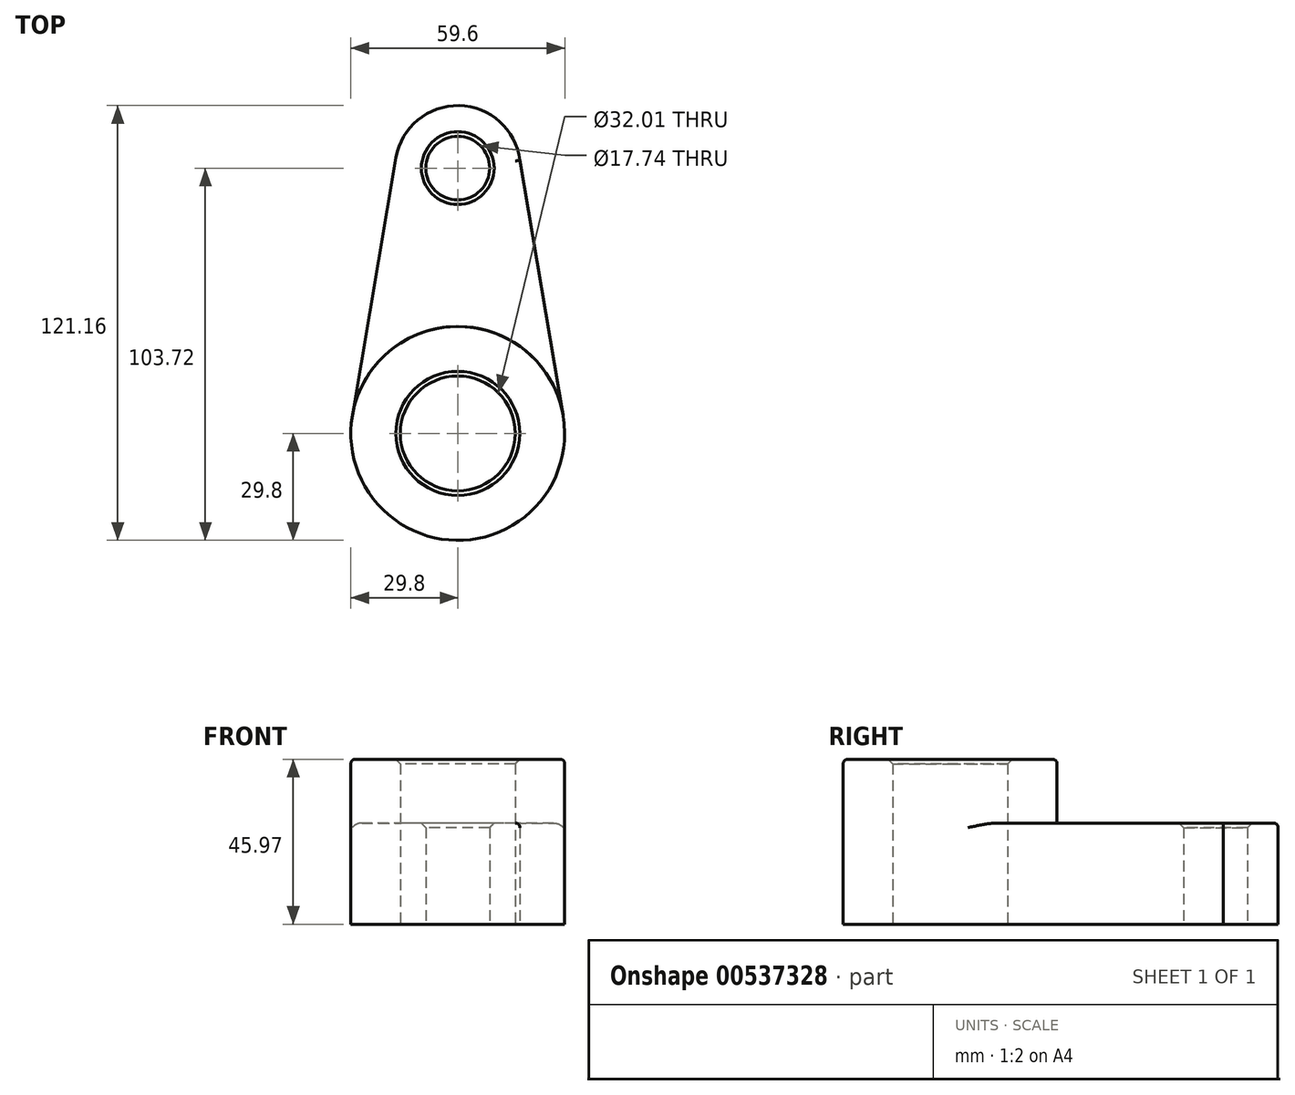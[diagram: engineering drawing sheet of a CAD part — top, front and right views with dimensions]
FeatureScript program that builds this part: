
annotation { "Feature Type Name" : "Feature", "Feature Type Description" : "" }
export const myFeature = defineFeature(function(context is Context, id is Id, definition is map)
    precondition{}
    {
        {
            var Q0;
            Q0=qCreatedBy(makeId("Top.planeOp"),FACE);
            var sketch = newSketch(context, id + "F0", { "sketchPlane" : qUnion([Q0])});
            skCircle(sketch, "E0", {"center": v(0, 0) * mm, "radius": 29.8 * mm});
            skCircle(sketch, "E1", {"center": v(0, 0) * mm, "radius": 16 * mm});
            skCircle(sketch, "E2", {"center": v(0, 73.92) * mm, "radius": 17.44 * mm});
            skCircle(sketch, "E3", {"center": v(0, 73.92) * mm, "radius": 8.87 * mm});
            skLineSegment(sketch, "E4", {"start": v(-29.38, 4.98) * mm, "end": v(-17.2, 76.84) * mm});
            skLineSegment(sketch, "E5", {"start": v(17.3, 76.1) * mm, "end": v(29.38, 4.99) * mm});
            skSolve(sketch);
        }
        {
            var Q0;
            Q0 = qSketchRegion(id + "F0", true);
            extrude(context, id + "F1", {"entities" : qUnion([Q0]), "depth" : 28.2 * mm, "offsetDistance" : 25.4 * mm});
        }
        {
            var Q0;
            Q0=makeQuery(id+"F0.imprint","IMPRINT",FACE,{"disambiguationData":[TD([[makeQuery(id+"F0.imprint","IMPRINT",EDGE,{"derivedFrom":sQuery(id+"F0.wireOp",EDGE,"E1")}),-1.0]])]});
            extrude(context, id + "F2", {"entities" : qUnion([Q0]), "operationType" : NewBodyOperationType.ADD, "depth" : 45.97 * mm, "offsetDistance" : 25.4 * mm});
        }
        {
            var Q0;
            Q0=makeQuery(id+"F2.opExtrude","CAP_EDGE",EDGE,{"disambiguationData":[OSD([sQuery(id+"F0.wireOp",EDGE,"E1")])],"isStart":false});
            chamfer(context, id + "F3", {"entities" : qUnion([Q0]), "width" : 1.27 * mm, "tangentPropagation" : true});
        }
        {
            var Q0;
            Q0=makeQuery(id+"F1.opExtrude","CAP_EDGE",EDGE,{"disambiguationData":[OSD([sQuery(id+"F0.wireOp",EDGE,"E3")])],"isStart":false});
            chamfer(context, id + "F4", {"entities" : qUnion([Q0]), "width" : 1.27 * mm, "tangentPropagation" : true});
        }
        {
            var Q0;
            Q0=makeQuery(id+"F2.opExtrude","CAP_EDGE",EDGE,{"disambiguationData":[OSD([sQuery(id+"F0.wireOp",EDGE,"E0")])],"isStart":false});
            var Q1;
            Q1=makeQuery(id+"F1.opExtrude","CAP_EDGE",EDGE,{"disambiguationData":[OSD([sQuery(id+"F0.wireOp",EDGE,"E5")])],"isStart":false});
            var Q2;
            Q2=makeQuery(id+"F1.opExtrude","CAP_EDGE",EDGE,{"disambiguationData":[OSD([sQuery(id+"F0.wireOp",EDGE,"E2")])],"isStart":false});
            var Q3;
            Q3=makeQuery(id+"F1.opExtrude","CAP_EDGE",EDGE,{"disambiguationData":[OSD([sQuery(id+"F0.wireOp",EDGE,"E4")])],"isStart":false});
            fillet(context, id + "F5", {"entities" : qUnion([Q0, Q1, Q2, Q3]), "radius" : 1.27 * mm, "tangentPropagation" : true, "allowEdgeOverflow" : false});
        }
    });
